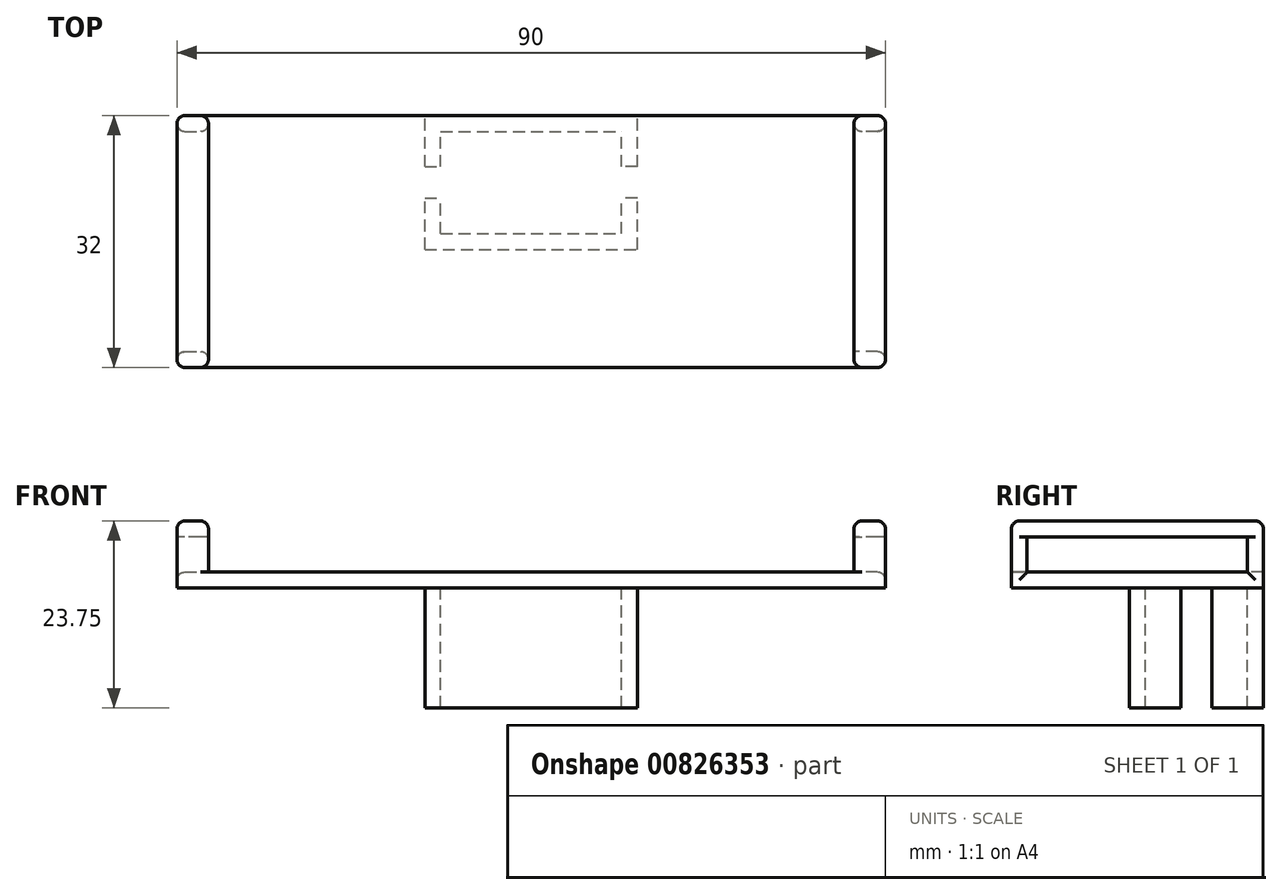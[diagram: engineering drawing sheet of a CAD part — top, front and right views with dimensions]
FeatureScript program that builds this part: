
annotation { "Feature Type Name" : "Feature", "Feature Type Description" : "" }
export const myFeature = defineFeature(function(context is Context, id is Id, definition is map)
    precondition{}
    {
        {
            var Q0;
            Q0=qCreatedBy(makeId("Top.planeOp"),FACE);
            var sketch = newSketch(context, id + "F0", { "sketchPlane" : qUnion([Q0])});
            skLineSegment(sketch, "E0.bottom", {"start": v(0, 0) * mm, "end": v(90, 0) * mm});
            skLineSegment(sketch, "E0.top", {"start": v(0, 32) * mm, "end": v(90, 32) * mm});
            skLineSegment(sketch, "E0.left", {"start": v(0, 0) * mm, "end": v(0, 32) * mm});
            skLineSegment(sketch, "E0.right", {"start": v(90, 0) * mm, "end": v(90, 32) * mm});
            skSolve(sketch);
        }
        {
            var Q0;
            Q0=makeQuery(id+"F0.imprint","IMPRINT",FACE,{"disambiguationData":[TD([[makeQuery(id+"F0.imprint","IMPRINT",EDGE,{"derivedFrom":sQuery(id+"F0.wireOp",EDGE,"E0.bottom")}),1.0]])]});
            extrude(context, id + "F1", {"entities" : qUnion([Q0]), "depth" : 2 * mm, "offsetDistance" : 25 * mm});
        }
        {
            var Q0;
            Q0=makeQuery(id+"F1.opExtrude","CAP_FACE",FACE,{"disambiguationData":[OSD([sQuery(id+"F0.wireOp",EDGE,"E0.bottom"),sQuery(id+"F0.wireOp",EDGE,"E0.top"),sQuery(id+"F0.wireOp",EDGE,"E0.left"),sQuery(id+"F0.wireOp",EDGE,"E0.right")])],"isStart":false});
            var sketch = newSketch(context, id + "F2", { "sketchPlane" : qUnion([Q0])});
            skLineSegment(sketch, "E1", {"start": v(0, 30) * mm, "end": v(4, 30) * mm});
            skLineSegment(sketch, "E2", {"start": v(4, 30) * mm, "end": v(4, 32) * mm});
            skLineSegment(sketch, "E3", {"start": v(45, 32) * mm, "end": v(45, 0) * mm, "construction": true});
            skLineSegment(sketch, "E4", {"start": v(0, 16) * mm, "end": v(90, 16) * mm, "construction": true});
            skLineSegment(sketch, "E5.MirrorCS", {"start": v(86, 30) * mm, "end": v(86, 32) * mm});
            skLineSegment(sketch, "E6.MirrorCS", {"start": v(90, 30) * mm, "end": v(86, 30) * mm});
            skLineSegment(sketch, "E7.MirrorCS", {"start": v(90, 2) * mm, "end": v(86, 2) * mm});
            skLineSegment(sketch, "E8.MirrorCS", {"start": v(86, 2) * mm, "end": v(86, 0) * mm});
            skLineSegment(sketch, "E9.MirrorCS", {"start": v(0, 2) * mm, "end": v(4, 2) * mm});
            skLineSegment(sketch, "E10.MirrorCS", {"start": v(4, 2) * mm, "end": v(4, 0) * mm});
            skSolve(sketch);
        }
        {
            var Q0;
            {var subQ0=sQuery(id+"F2.wireOp",EDGE,"E1");Q0=makeQuery(id+"F2.imprint","IMPRINT",FACE,{"disambiguationData":[TD([[makeQuery(id+"F2.imprint","IMPRINT",EDGE,{"derivedFrom":subQ0}),1.0]])]});}
            var Q1;
            {var subQ0=sQuery(id+"F2.wireOp",EDGE,"E9.MirrorCS");Q1=makeQuery(id+"F2.imprint","IMPRINT",FACE,{"disambiguationData":[TD([[makeQuery(id+"F2.imprint","IMPRINT",EDGE,{"derivedFrom":subQ0}),-1.0]])]});}
            var Q2;
            {var subQ0=sQuery(id+"F2.wireOp",EDGE,"E7.MirrorCS");Q2=makeQuery(id+"F2.imprint","IMPRINT",FACE,{"disambiguationData":[TD([[makeQuery(id+"F2.imprint","IMPRINT",EDGE,{"derivedFrom":subQ0}),1.0]])]});}
            var Q3;
            {var subQ0=sQuery(id+"F2.wireOp",EDGE,"E5.MirrorCS");Q3=makeQuery(id+"F2.imprint","IMPRINT",FACE,{"disambiguationData":[TD([[makeQuery(id+"F2.imprint","IMPRINT",EDGE,{"derivedFrom":subQ0}),-1.0]])]});}
            extrude(context, id + "F3", {"entities" : qUnion([Q0, Q1, Q2, Q3]), "operationType" : NewBodyOperationType.ADD, "depth" : 6.5 * mm, "offsetDistance" : 25 * mm});
        }
        {
            var Q0;
            Q0=makeQuery(id+"F3.opExtrude","SWEPT_FACE",FACE,{"disambiguationData":[OSD([sQuery(id+"F2.wireOp",EDGE,"E7.MirrorCS")])]});
            var sketch = newSketch(context, id + "F4", { "sketchPlane" : qUnion([Q0])});
            skLineSegment(sketch, "E11.bottom", {"start": v(-90, 8.5) * mm, "end": v(-86, 8.5) * mm});
            skLineSegment(sketch, "E11.top", {"start": v(-90, 6.5) * mm, "end": v(-86, 6.5) * mm});
            skLineSegment(sketch, "E11.left", {"start": v(-90, 8.5) * mm, "end": v(-90, 6.5) * mm});
            skLineSegment(sketch, "E11.right", {"start": v(-86, 8.5) * mm, "end": v(-86, 6.5) * mm});
            skSolve(sketch);
        }
        {
            var Q0;
            Q0=makeQuery(id+"F3.opExtrude","SWEPT_FACE",FACE,{"disambiguationData":[OSD([sQuery(id+"F2.wireOp",EDGE,"E9.MirrorCS")])]});
            var sketch = newSketch(context, id + "F5", { "sketchPlane" : qUnion([Q0])});
            skLineSegment(sketch, "E12.bottom", {"start": v(-4, 8.5) * mm, "end": v(0, 8.5) * mm});
            skLineSegment(sketch, "E12.top", {"start": v(-4, 6.5) * mm, "end": v(0, 6.5) * mm});
            skLineSegment(sketch, "E12.left", {"start": v(-4, 8.5) * mm, "end": v(-4, 6.5) * mm});
            skLineSegment(sketch, "E12.right", {"start": v(0, 8.5) * mm, "end": v(0, 6.5) * mm});
            skSolve(sketch);
        }
        {
            var Q0;
            Q0=makeQuery(id+"F5.imprint","IMPRINT",FACE,{"disambiguationData":[TD([[makeQuery(id+"F5.imprint","IMPRINT",EDGE,{"derivedFrom":sQuery(id+"F5.wireOp",EDGE,"E12.bottom")}),1.0]])]});
            extrude(context, id + "F6", {"entities" : qUnion([Q0]), "operationType" : NewBodyOperationType.ADD, "depth" : 28 * mm, "offsetDistance" : 25 * mm});
        }
        {
            var Q0;
            Q0=makeQuery(id+"F4.imprint","IMPRINT",FACE,{"disambiguationData":[TD([[makeQuery(id+"F4.imprint","IMPRINT",EDGE,{"derivedFrom":sQuery(id+"F4.wireOp",EDGE,"E11.bottom")}),-1.0]])]});
            extrude(context, id + "F7", {"entities" : qUnion([Q0]), "operationType" : NewBodyOperationType.ADD, "depth" : 28 * mm, "offsetDistance" : 25 * mm});
        }
        {
            var Q0;
            {var subQ0=sQuery(id+"F0.wireOp",EDGE,"E0.left");var subQ1=makeQuery(id+"F1.opExtrude","CAP_EDGE",EDGE,{"disambiguationData":[OSD([subQ0])],"isStart":false});Q0=makeQuery(id+"F6.boolean.opBoolean","MERGE",EDGE,{"derivedFrom":[makeQuery(id+"F3.opExtrude","CAP_EDGE",EDGE,{"disambiguationData":[OSD([subQ0]),TDD([makeQuery(id+"F2.imprint","IMPRINT",EDGE,{"disambiguationData":[TD([[makeQuery(id+"F2.imprint","INTERSECT",VERTEX,{"derivedFrom":[makeQuery(id+"F1.opExtrude","CAP_EDGE",EDGE,{"disambiguationData":[OSD([sQuery(id+"F0.wireOp",EDGE,"E0.bottom")])],"isStart":false}),subQ1]}),-1.0]])],"derivedFrom":subQ1})])],"isStart":false}),makeQuery(id+"F3.opExtrude","CAP_EDGE",EDGE,{"disambiguationData":[OSD([subQ0]),TDD([makeQuery(id+"F2.imprint","IMPRINT",EDGE,{"disambiguationData":[TD([[makeQuery(id+"F2.imprint","INTERSECT",VERTEX,{"derivedFrom":[makeQuery(id+"F1.opExtrude","CAP_EDGE",EDGE,{"disambiguationData":[OSD([sQuery(id+"F0.wireOp",EDGE,"E0.top")])],"isStart":false}),subQ1]}),1.0]])],"derivedFrom":subQ1})])],"isStart":false}),makeQuery(id+"F6.opExtrude","SWEPT_EDGE",EDGE,{"disambiguationData":[OSD([sQuery(id+"F5.wireOp",EDGE,"E12.bottom"),sQuery(id+"F5.wireOp",EDGE,"E12.right")])]})]});}
            var Q1;
            Q1=makeQuery(id+"F6.boolean.opBoolean","MERGE",EDGE,{"derivedFrom":[makeQuery(id+"F3.opExtrude","CAP_EDGE",EDGE,{"disambiguationData":[OSD([sQuery(id+"F2.wireOp",EDGE,"E2")])],"isStart":false}),makeQuery(id+"F3.opExtrude","CAP_EDGE",EDGE,{"disambiguationData":[OSD([sQuery(id+"F2.wireOp",EDGE,"E10.MirrorCS")])],"isStart":false}),makeQuery(id+"F6.opExtrude","SWEPT_EDGE",EDGE,{"disambiguationData":[OSD([sQuery(id+"F5.wireOp",EDGE,"E12.bottom"),sQuery(id+"F5.wireOp",EDGE,"E12.left")])]})]});
            var Q2;
            {var subQ0=sQuery(id+"F0.wireOp",EDGE,"E0.left");var subQ1=sQuery(id+"F0.wireOp",EDGE,"E0.top");Q2=makeQuery(id+"F3.boolean.opBoolean","MERGE",EDGE,{"derivedFrom":[makeQuery(id+"F1.opExtrude","SWEPT_EDGE",EDGE,{"disambiguationData":[OSD([subQ1,subQ0])]}),makeQuery(id+"F3.opExtrude","SWEPT_EDGE",EDGE,{"disambiguationData":[OSD([subQ1,subQ0])]})]});}
            var Q3;
            {var subQ0=sQuery(id+"F0.wireOp",EDGE,"E0.left");var subQ1=sQuery(id+"F0.wireOp",EDGE,"E0.bottom");Q3=makeQuery(id+"F3.boolean.opBoolean","MERGE",EDGE,{"derivedFrom":[makeQuery(id+"F1.opExtrude","SWEPT_EDGE",EDGE,{"disambiguationData":[OSD([subQ1,subQ0])]}),makeQuery(id+"F3.opExtrude","SWEPT_EDGE",EDGE,{"disambiguationData":[OSD([subQ1,subQ0])]})]});}
            var Q4;
            Q4=makeQuery(id+"F1.opExtrude","CAP_EDGE",EDGE,{"disambiguationData":[OSD([sQuery(id+"F0.wireOp",EDGE,"E0.left")])],"isStart":false});
            var Q5;
            {var subQ0=sQuery(id+"F0.wireOp",EDGE,"E0.top");var subQ1=makeQuery(id+"F1.opExtrude","CAP_EDGE",EDGE,{"disambiguationData":[OSD([subQ0])],"isStart":false});Q5=makeQuery(id+"F3.opExtrude","CAP_EDGE",EDGE,{"disambiguationData":[OSD([subQ0]),TDD([makeQuery(id+"F2.imprint","IMPRINT",EDGE,{"disambiguationData":[TD([[makeQuery(id+"F2.imprint","INTERSECT",VERTEX,{"derivedFrom":[subQ1,makeQuery(id+"F1.opExtrude","CAP_EDGE",EDGE,{"disambiguationData":[OSD([sQuery(id+"F0.wireOp",EDGE,"E0.left")])],"isStart":false})]}),-1.0]])],"derivedFrom":subQ1})])],"isStart":false});}
            var Q6;
            {var subQ0=sQuery(id+"F0.wireOp",EDGE,"E0.bottom");var subQ1=makeQuery(id+"F1.opExtrude","CAP_EDGE",EDGE,{"disambiguationData":[OSD([subQ0])],"isStart":false});Q6=makeQuery(id+"F3.opExtrude","CAP_EDGE",EDGE,{"disambiguationData":[OSD([subQ0]),TDD([makeQuery(id+"F2.imprint","IMPRINT",EDGE,{"disambiguationData":[TD([[makeQuery(id+"F2.imprint","INTERSECT",VERTEX,{"derivedFrom":[subQ1,makeQuery(id+"F1.opExtrude","CAP_EDGE",EDGE,{"disambiguationData":[OSD([sQuery(id+"F0.wireOp",EDGE,"E0.left")])],"isStart":false})]}),-1.0]])],"derivedFrom":subQ1})])],"isStart":false});}
            var Q7;
            Q7=makeQuery(id+"F3.opExtrude","SWEPT_EDGE",EDGE,{"disambiguationData":[OSD([sQuery(id+"F0.wireOp",EDGE,"E0.left"),sQuery(id+"F2.wireOp",EDGE,"E1")])]});
            var Q8;
            Q8=makeQuery(id+"F3.opExtrude","SWEPT_EDGE",EDGE,{"disambiguationData":[OSD([sQuery(id+"F0.wireOp",EDGE,"E0.left"),sQuery(id+"F2.wireOp",EDGE,"E9.MirrorCS")])]});
            var Q9;
            Q9=makeQuery(id+"F3.opExtrude","SWEPT_EDGE",EDGE,{"disambiguationData":[OSD([sQuery(id+"F2.wireOp",EDGE,"E9.MirrorCS"),sQuery(id+"F2.wireOp",EDGE,"E10.MirrorCS")])]});
            var Q10;
            Q10=makeQuery(id+"F3.opExtrude","SWEPT_EDGE",EDGE,{"disambiguationData":[OSD([sQuery(id+"F2.wireOp",EDGE,"E1"),sQuery(id+"F2.wireOp",EDGE,"E2")])]});
            var Q11;
            Q11=makeQuery(id+"F3.opExtrude","SWEPT_EDGE",EDGE,{"disambiguationData":[OSD([sQuery(id+"F0.wireOp",EDGE,"E0.top"),sQuery(id+"F2.wireOp",EDGE,"E2")])]});
            var Q12;
            Q12=makeQuery(id+"F3.opExtrude","SWEPT_EDGE",EDGE,{"disambiguationData":[OSD([sQuery(id+"F0.wireOp",EDGE,"E0.bottom"),sQuery(id+"F2.wireOp",EDGE,"E10.MirrorCS")])]});
            var Q13;
            Q13=makeQuery(id+"F3.opExtrude","SWEPT_EDGE",EDGE,{"disambiguationData":[OSD([sQuery(id+"F0.wireOp",EDGE,"E0.bottom"),sQuery(id+"F2.wireOp",EDGE,"E8.MirrorCS")])]});
            var Q14;
            {var subQ0=sQuery(id+"F0.wireOp",EDGE,"E0.right");var subQ1=sQuery(id+"F0.wireOp",EDGE,"E0.bottom");Q14=makeQuery(id+"F3.boolean.opBoolean","MERGE",EDGE,{"derivedFrom":[makeQuery(id+"F1.opExtrude","SWEPT_EDGE",EDGE,{"disambiguationData":[OSD([subQ1,subQ0])]}),makeQuery(id+"F3.opExtrude","SWEPT_EDGE",EDGE,{"disambiguationData":[OSD([subQ1,subQ0])]})]});}
            var Q15;
            Q15=makeQuery(id+"F3.opExtrude","SWEPT_EDGE",EDGE,{"disambiguationData":[OSD([sQuery(id+"F2.wireOp",EDGE,"E5.MirrorCS"),sQuery(id+"F2.wireOp",EDGE,"E6.MirrorCS")])]});
            var Q16;
            Q16=makeQuery(id+"F3.opExtrude","SWEPT_EDGE",EDGE,{"disambiguationData":[OSD([sQuery(id+"F0.wireOp",EDGE,"E0.right"),sQuery(id+"F2.wireOp",EDGE,"E6.MirrorCS")])]});
            var Q17;
            Q17=makeQuery(id+"F3.opExtrude","SWEPT_EDGE",EDGE,{"disambiguationData":[OSD([sQuery(id+"F0.wireOp",EDGE,"E0.top"),sQuery(id+"F2.wireOp",EDGE,"E5.MirrorCS")])]});
            var Q18;
            {var subQ0=sQuery(id+"F0.wireOp",EDGE,"E0.right");var subQ1=sQuery(id+"F0.wireOp",EDGE,"E0.top");Q18=makeQuery(id+"F3.boolean.opBoolean","MERGE",EDGE,{"derivedFrom":[makeQuery(id+"F1.opExtrude","SWEPT_EDGE",EDGE,{"disambiguationData":[OSD([subQ1,subQ0])]}),makeQuery(id+"F3.opExtrude","SWEPT_EDGE",EDGE,{"disambiguationData":[OSD([subQ1,subQ0])]})]});}
            var Q19;
            {var subQ0=sQuery(id+"F0.wireOp",EDGE,"E0.right");var subQ1=makeQuery(id+"F1.opExtrude","CAP_EDGE",EDGE,{"disambiguationData":[OSD([subQ0])],"isStart":false});Q19=makeQuery(id+"F7.boolean.opBoolean","MERGE",EDGE,{"derivedFrom":[makeQuery(id+"F3.opExtrude","CAP_EDGE",EDGE,{"disambiguationData":[OSD([subQ0]),TDD([makeQuery(id+"F2.imprint","IMPRINT",EDGE,{"disambiguationData":[TD([[makeQuery(id+"F2.imprint","INTERSECT",VERTEX,{"derivedFrom":[makeQuery(id+"F1.opExtrude","CAP_EDGE",EDGE,{"disambiguationData":[OSD([sQuery(id+"F0.wireOp",EDGE,"E0.bottom")])],"isStart":false}),subQ1]}),-1.0]])],"derivedFrom":subQ1})])],"isStart":false}),makeQuery(id+"F3.opExtrude","CAP_EDGE",EDGE,{"disambiguationData":[OSD([subQ0]),TDD([makeQuery(id+"F2.imprint","IMPRINT",EDGE,{"disambiguationData":[TD([[makeQuery(id+"F2.imprint","INTERSECT",VERTEX,{"derivedFrom":[makeQuery(id+"F1.opExtrude","CAP_EDGE",EDGE,{"disambiguationData":[OSD([sQuery(id+"F0.wireOp",EDGE,"E0.top")])],"isStart":false}),subQ1]}),1.0]])],"derivedFrom":subQ1})])],"isStart":false}),makeQuery(id+"F7.opExtrude","SWEPT_EDGE",EDGE,{"disambiguationData":[OSD([sQuery(id+"F4.wireOp",EDGE,"E11.bottom"),sQuery(id+"F4.wireOp",EDGE,"E11.left")])]})]});}
            var Q20;
            Q20=makeQuery(id+"F7.boolean.opBoolean","MERGE",EDGE,{"derivedFrom":[makeQuery(id+"F3.opExtrude","CAP_EDGE",EDGE,{"disambiguationData":[OSD([sQuery(id+"F2.wireOp",EDGE,"E5.MirrorCS")])],"isStart":false}),makeQuery(id+"F3.opExtrude","CAP_EDGE",EDGE,{"disambiguationData":[OSD([sQuery(id+"F2.wireOp",EDGE,"E8.MirrorCS")])],"isStart":false}),makeQuery(id+"F7.opExtrude","SWEPT_EDGE",EDGE,{"disambiguationData":[OSD([sQuery(id+"F4.wireOp",EDGE,"E11.bottom"),sQuery(id+"F4.wireOp",EDGE,"E11.right")])]})]});
            var Q21;
            {var subQ0=sQuery(id+"F0.wireOp",EDGE,"E0.bottom");var subQ1=makeQuery(id+"F1.opExtrude","CAP_EDGE",EDGE,{"disambiguationData":[OSD([subQ0])],"isStart":false});Q21=makeQuery(id+"F3.opExtrude","CAP_EDGE",EDGE,{"disambiguationData":[OSD([subQ0]),TDD([makeQuery(id+"F2.imprint","IMPRINT",EDGE,{"disambiguationData":[TD([[makeQuery(id+"F2.imprint","INTERSECT",VERTEX,{"derivedFrom":[subQ1,makeQuery(id+"F1.opExtrude","CAP_EDGE",EDGE,{"disambiguationData":[OSD([sQuery(id+"F0.wireOp",EDGE,"E0.right")])],"isStart":false})]}),1.0]])],"derivedFrom":subQ1})])],"isStart":false});}
            var Q22;
            {var subQ0=sQuery(id+"F0.wireOp",EDGE,"E0.top");var subQ1=makeQuery(id+"F1.opExtrude","CAP_EDGE",EDGE,{"disambiguationData":[OSD([subQ0])],"isStart":false});Q22=makeQuery(id+"F3.opExtrude","CAP_EDGE",EDGE,{"disambiguationData":[OSD([subQ0]),TDD([makeQuery(id+"F2.imprint","IMPRINT",EDGE,{"disambiguationData":[TD([[makeQuery(id+"F2.imprint","INTERSECT",VERTEX,{"derivedFrom":[subQ1,makeQuery(id+"F1.opExtrude","CAP_EDGE",EDGE,{"disambiguationData":[OSD([sQuery(id+"F0.wireOp",EDGE,"E0.right")])],"isStart":false})]}),1.0]])],"derivedFrom":subQ1})])],"isStart":false});}
            var Q23;
            Q23=makeQuery(id+"F3.opExtrude","SWEPT_EDGE",EDGE,{"disambiguationData":[OSD([sQuery(id+"F0.wireOp",EDGE,"E0.right"),sQuery(id+"F2.wireOp",EDGE,"E7.MirrorCS")])]});
            var Q24;
            Q24=makeQuery(id+"F1.opExtrude","CAP_EDGE",EDGE,{"disambiguationData":[OSD([sQuery(id+"F0.wireOp",EDGE,"E0.right")])],"isStart":false});
            fillet(context, id + "F8", {"entities" : qUnion([Q0, Q1, Q2, Q3, Q4, Q5, Q6, Q7, Q8, Q9, Q10, Q11, Q12, Q13, Q14, Q15, Q16, Q17, Q18, Q19, Q20, Q21, Q22, Q23, Q24]), "radius" : 1 * mm, "tangentPropagation" : true, "allowEdgeOverflow" : false});
        }
        {
            var Q0;
            Q0=makeQuery(id+"F1.opExtrude","CAP_FACE",FACE,{"disambiguationData":[OSD([sQuery(id+"F0.wireOp",EDGE,"E0.bottom"),sQuery(id+"F0.wireOp",EDGE,"E0.top"),sQuery(id+"F0.wireOp",EDGE,"E0.left"),sQuery(id+"F0.wireOp",EDGE,"E0.right")])],"isStart":true});
            var sketch = newSketch(context, id + "F9", { "sketchPlane" : qUnion([Q0])});
            skLineSegment(sketch, "E13.bottom", {"start": v(33.5, -17) * mm, "end": v(56.5, -17) * mm});
            skLineSegment(sketch, "E13.top", {"start": v(33.5, -30) * mm, "end": v(56.5, -30) * mm});
            skLineSegment(sketch, "E13.left", {"start": v(33.5, -17) * mm, "end": v(33.5, -30) * mm});
            skLineSegment(sketch, "E13.right", {"start": v(56.5, -17) * mm, "end": v(56.5, -30) * mm});
            skLineSegment(sketch, "E14.0", {"start": v(31.5, -15) * mm, "end": v(58.5, -15) * mm});
            skLineSegment(sketch, "E14.1", {"start": v(31.5, -15) * mm, "end": v(31.5, -32) * mm});
            skLineSegment(sketch, "E14.2", {"start": v(31.5, -32) * mm, "end": v(58.5, -32) * mm});
            skLineSegment(sketch, "E14.3", {"start": v(58.5, -15) * mm, "end": v(58.5, -32) * mm});
            skArc(sketch, "E15.0", {"start": v(1, 5) * mm, "mid": v(-3.24, 3.24) * mm, "end": v(-5, -1) * mm});
            skLineSegment(sketch, "E15.1", {"start": v(89, 5) * mm, "end": v(1, 5) * mm});
            skLineSegment(sketch, "E15.2", {"start": v(-5, -1) * mm, "end": v(-5, -31) * mm});
            skArc(sketch, "E15.3", {"start": v(95, -1) * mm, "mid": v(93.24, 3.24) * mm, "end": v(89, 5) * mm});
            skArc(sketch, "E15.4", {"start": v(-5, -31) * mm, "mid": v(-3.24, -35.24) * mm, "end": v(1, -37) * mm});
            skLineSegment(sketch, "E15.5", {"start": v(1, -37) * mm, "end": v(89, -37) * mm});
            skArc(sketch, "E15.6", {"start": v(89, -37) * mm, "mid": v(93.24, -35.24) * mm, "end": v(95, -31) * mm});
            skLineSegment(sketch, "E15.7", {"start": v(95, -31) * mm, "end": v(95, -1) * mm});
            skLineSegment(sketch, "E16", {"start": v(58.5, -23.5) * mm, "end": v(31.5, -23.5) * mm, "construction": true});
            skLineSegment(sketch, "E17.bottom", {"start": v(31.5, -21.5) * mm, "end": v(33.5, -21.5) * mm});
            skLineSegment(sketch, "E17.top", {"start": v(31.5, -25.5) * mm, "end": v(33.5, -25.5) * mm});
            skLineSegment(sketch, "E17.left", {"start": v(31.5, -21.5) * mm, "end": v(31.5, -25.5) * mm});
            skLineSegment(sketch, "E17.right", {"start": v(33.5, -21.5) * mm, "end": v(33.5, -25.5) * mm});
            skLineSegment(sketch, "E18", {"start": v(45, -15) * mm, "end": v(45, -32) * mm, "construction": true});
            skLineSegment(sketch, "E19.MirrorCS", {"start": v(58.5, -21.5) * mm, "end": v(56.5, -21.5) * mm});
            skLineSegment(sketch, "E20.MirrorCS", {"start": v(58.5, -25.5) * mm, "end": v(56.5, -25.5) * mm});
            skSolve(sketch);
        }
        {
            var Q0;
            {var subQ5=sQuery(id+"F9.wireOp",EDGE,"E13.top");Q0=makeQuery(id+"F9.imprint","IMPRINT",FACE,{"disambiguationData":[TD([[makeQuery(id+"F9.imprint","IMPRINT",EDGE,{"derivedFrom":subQ5}),-1.0]])]});}
            var Q1;
            {var subQ1=sQuery(id+"F9.wireOp",EDGE,"E13.bottom");Q1=makeQuery(id+"F9.imprint","IMPRINT",FACE,{"disambiguationData":[TD([[makeQuery(id+"F9.imprint","IMPRINT",EDGE,{"derivedFrom":subQ1}),1.0]])]});}
            extrude(context, id + "F10", {"entities" : qUnion([Q0, Q1]), "operationType" : NewBodyOperationType.ADD, "depth" : 15.25 * mm, "offsetDistance" : 25 * mm});
        }
    });
